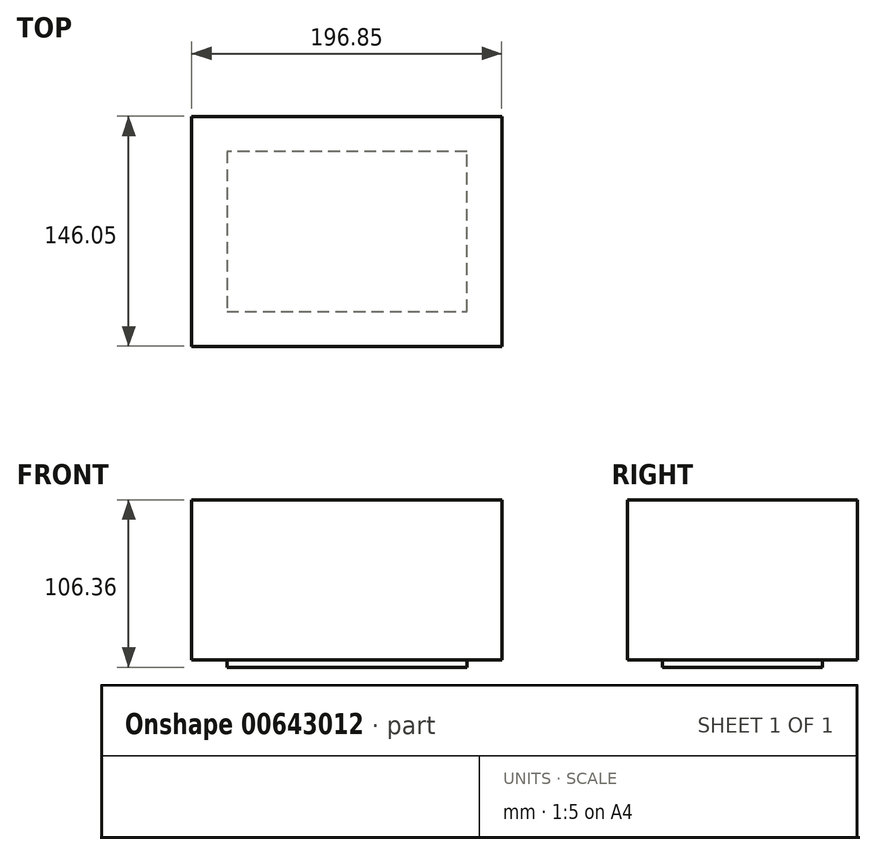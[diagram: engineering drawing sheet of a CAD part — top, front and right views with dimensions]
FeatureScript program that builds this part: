
annotation { "Feature Type Name" : "Feature", "Feature Type Description" : "" }
export const myFeature = defineFeature(function(context is Context, id is Id, definition is map)
    precondition{}
    {
        {
            var Q0;
            Q0=qCreatedBy(makeId("Top.planeOp"),FACE);
            var sketch = newSketch(context, id + "F0", { "sketchPlane" : qUnion([Q0])});
            skLineSegment(sketch, "E0", {"start": v(-76.61, 0) * mm, "end": v(75.79, 0) * mm});
            skLineSegment(sketch, "E1", {"start": v(75.79, 0) * mm, "end": v(75.79, 101.6) * mm});
            skLineSegment(sketch, "E2", {"start": v(75.79, 101.6) * mm, "end": v(-76.61, 101.6) * mm});
            skLineSegment(sketch, "E3", {"start": v(-76.61, 101.6) * mm, "end": v(-76.61, 0) * mm});
            skSolve(sketch);
        }
        {
            var Q0;
            Q0 = qSketchRegion(id + "F0", true);
            extrude(context, id + "F1", {"entities" : qUnion([Q0]), "depth" : 4.76 * mm, "offsetDistance" : 25.4 * mm});
        }
        {
            var Q0;
            Q0=makeQuery(id+"F1.opExtrude","CAP_FACE",FACE,{"disambiguationData":[OSD([sQuery(id+"F0.wireOp",EDGE,"E0"),sQuery(id+"F0.wireOp",EDGE,"E1"),sQuery(id+"F0.wireOp",EDGE,"E2"),sQuery(id+"F0.wireOp",EDGE,"E3")])],"isStart":false});
            var sketch = newSketch(context, id + "F2", { "sketchPlane" : qUnion([Q0])});
            skLineSegment(sketch, "E4", {"start": v(0, 0) * mm, "end": v(-0.41, -22.22) * mm});
            skPoint(sketch, "E4.endSnap0", {"position": v(-0.41, 0) * mm});
            skLineSegment(sketch, "E5", {"start": v(-76.61, 50.8) * mm, "end": v(-98.84, 50.8) * mm});
            skPoint(sketch, "E5.endSnap0", {"position": v(-76.61, 50.8) * mm});
            skLineSegment(sketch, "E6", {"start": v(0, 101.6) * mm, "end": v(0, 123.82) * mm});
            skLineSegment(sketch, "E7", {"start": v(75.79, 50.8) * mm, "end": v(98.01, 50.8) * mm});
            skPoint(sketch, "E8.endSnap0", {"position": v(-87.72, 50.8) * mm});
            skLineSegment(sketch, "E9", {"start": v(-98.84, 50.8) * mm, "end": v(-98.84, 123.82) * mm});
            skLineSegment(sketch, "E10", {"start": v(-98.84, 123.82) * mm, "end": v(0, 123.82) * mm});
            skLineSegment(sketch, "E11", {"start": v(98.01, 50.8) * mm, "end": v(98.01, 123.82) * mm});
            skLineSegment(sketch, "E12", {"start": v(98.01, 123.82) * mm, "end": v(0, 123.82) * mm});
            skLineSegment(sketch, "E13", {"start": v(98.01, 50.8) * mm, "end": v(98.01, -22.22) * mm});
            skLineSegment(sketch, "E14", {"start": v(98.01, -22.22) * mm, "end": v(-0.41, -22.22) * mm});
            skLineSegment(sketch, "E15", {"start": v(-98.84, 50.8) * mm, "end": v(-98.84, -22.22) * mm});
            skLineSegment(sketch, "E16", {"start": v(-98.84, -22.22) * mm, "end": v(-0.41, -22.22) * mm});
            skSolve(sketch);
        }
        {
            var Q0;
            Q0 = qSketchRegion(id + "F2", true);
            extrude(context, id + "F3", {"entities" : qUnion([Q0]), "operationType" : NewBodyOperationType.ADD, "depth" : 101.6 * mm, "offsetDistance" : 25.4 * mm});
        }
    });
